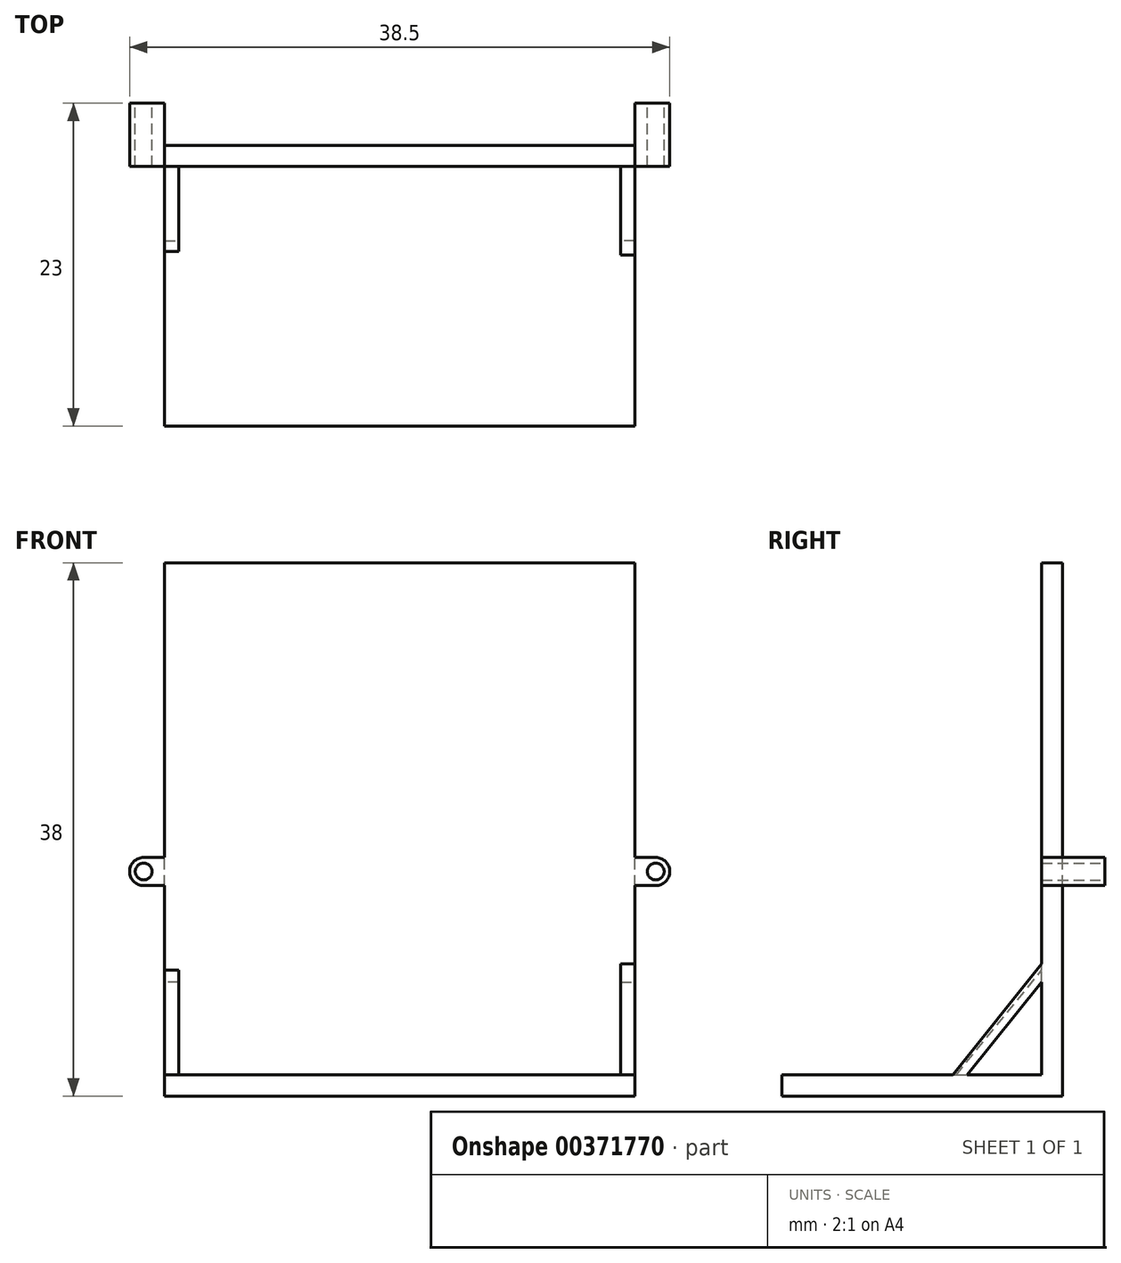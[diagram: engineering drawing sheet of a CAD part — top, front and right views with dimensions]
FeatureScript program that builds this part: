
annotation { "Feature Type Name" : "Feature", "Feature Type Description" : "" }
export const myFeature = defineFeature(function(context is Context, id is Id, definition is map)
    precondition{}
    {
        {
            var Q0;
            Q0=qCreatedBy(makeId("Front.planeOp"),FACE);
            var sketch = newSketch(context, id + "F0", { "sketchPlane" : qUnion([Q0])});
            skLineSegment(sketch, "E0.bottom", {"start": v(0, 0) * mm, "end": v(-33.5, 0) * mm});
            skLineSegment(sketch, "E0.top", {"start": v(0, 38) * mm, "end": v(-33.5, 38) * mm});
            skLineSegment(sketch, "E0.left", {"start": v(0, 0) * mm, "end": v(0, 38) * mm});
            skLineSegment(sketch, "E0.right", {"start": v(-33.5, 0) * mm, "end": v(-33.5, 38) * mm});
            skArc(sketch, "E1", {"start": v(-35, 17) * mm, "mid": v(-36, 16) * mm, "end": v(-35, 15) * mm});
            skLineSegment(sketch, "E2", {"start": v(-35, 17) * mm, "end": v(-33.5, 17) * mm});
            skLineSegment(sketch, "E3", {"start": v(-35, 15) * mm, "end": v(-33.5, 15) * mm});
            skLineSegment(sketch, "E4", {"start": v(-33.5, 15) * mm, "end": v(1.5, 15) * mm});
            skLineSegment(sketch, "E5", {"start": v(-33.5, 17) * mm, "end": v(1.5, 17) * mm});
            skArc(sketch, "E6", {"start": v(1.5, 15) * mm, "mid": v(2.5, 16) * mm, "end": v(1.5, 17) * mm});
            skCircle(sketch, "E7", {"center": v(1.5, 16) * mm, "radius": 0.6 * mm});
            skCircle(sketch, "E8", {"center": v(-35, 16) * mm, "radius": 0.6 * mm});
            skSolve(sketch);
        }
        {
            var Q0;
            Q0=qCreatedBy(makeId("Top.planeOp"),FACE);
            var sketch = newSketch(context, id + "F1", { "sketchPlane" : qUnion([Q0])});
            skLineSegment(sketch, "E9.bottom", {"start": v(-33.5, 0) * mm, "end": v(0, 0) * mm});
            skLineSegment(sketch, "E9.top", {"start": v(-33.5, -20) * mm, "end": v(0, -20) * mm});
            skLineSegment(sketch, "E9.left", {"start": v(-33.5, 0) * mm, "end": v(-33.5, -20) * mm});
            skLineSegment(sketch, "E9.right", {"start": v(0, 0) * mm, "end": v(0, -20) * mm});
            skSolve(sketch);
        }
        {
            var Q0;
            Q0=qCreatedBy(makeId("Right.planeOp"),FACE);
            var sketch = newSketch(context, id + "F2", { "sketchPlane" : qUnion([Q0])});
            skLineSegment(sketch, "E10", {"start": v(-8, 0) * mm, "end": v(0, 10) * mm});
            skLineSegment(sketch, "E11", {"start": v(0, 10) * mm, "end": v(0, 11.28) * mm});
            skLineSegment(sketch, "E12", {"start": v(0, 11.28) * mm, "end": v(-9.02, 0) * mm});
            skLineSegment(sketch, "E13", {"start": v(0, 11.28) * mm, "end": v(0, 10) * mm});
            skLineSegment(sketch, "E14", {"start": v(-8, 0) * mm, "end": v(-9.02, 0) * mm});
            skSolve(sketch);
        }
        {
            var Q0;
            {var subQ0=sQuery(id+"F0.wireOp",EDGE,"E0.top");Q0=makeQuery(id+"F0.imprint","IMPRINT",FACE,{"disambiguationData":[TD([[makeQuery(id+"F0.imprint","IMPRINT",EDGE,{"derivedFrom":subQ0}),1.0]])]});}
            var Q1;
            {var subQ0=sQuery(id+"F0.wireOp",EDGE,"E4");var subQ1=sQuery(id+"F0.wireOp",EDGE,"E0.left");var subQ2=makeQuery(id+"F0.imprint","INTERSECT",VERTEX,{"derivedFrom":[subQ1,subQ0]});Q1=makeQuery(id+"F0.imprint","IMPRINT",FACE,{"disambiguationData":[TD([[makeQuery(id+"F0.imprint","IMPRINT",EDGE,{"disambiguationData":[TD([[subQ2,-1.0]])],"derivedFrom":subQ1}),1.0]])]});}
            var Q2;
            {var subQ0=sQuery(id+"F0.wireOp",EDGE,"E0.bottom");Q2=makeQuery(id+"F0.imprint","IMPRINT",FACE,{"disambiguationData":[TD([[makeQuery(id+"F0.imprint","IMPRINT",EDGE,{"derivedFrom":subQ0}),-1.0]])]});}
            var Q3;
            Q3=makeQuery(id+"F0.imprint","IMPRINT",FACE,{"disambiguationData":[TD([[makeQuery(id+"F0.imprint","IMPRINT",EDGE,{"derivedFrom":sQuery(id+"F0.wireOp",EDGE,"E1")}),1.0]])]});
            var Q4;
            {var subQ0=sQuery(id+"F0.wireOp",EDGE,"E6");Q4=makeQuery(id+"F0.imprint","IMPRINT",FACE,{"disambiguationData":[TD([[makeQuery(id+"F0.imprint","IMPRINT",EDGE,{"derivedFrom":subQ0}),1.0]])]});}
            extrude(context, id + "F3", {"entities" : qUnion([Q0, Q1, Q2, Q3, Q4]), "depth" : 1.5 * mm});
        }
        {
            var Q0;
            Q0=makeQuery(id+"F1.imprint","IMPRINT",FACE,{"disambiguationData":[TD([[makeQuery(id+"F1.imprint","IMPRINT",EDGE,{"derivedFrom":sQuery(id+"F1.wireOp",EDGE,"E9.bottom")}),-1.0]])]});
            extrude(context, id + "F4", {"entities" : qUnion([Q0]), "operationType" : NewBodyOperationType.ADD, "depth" : 1.5 * mm});
        }
        {
            var Q0;
            Q0 = qSketchRegion(id + "F2", true);
            extrude(context, id + "F5", {"entities" : qUnion([Q0]), "operationType" : NewBodyOperationType.ADD, "oppositeDirection" : true, "depth" : 1 * mm});
        }
        {
            var Q0;
            Q0=qCreatedBy(makeId("Right.planeOp"),FACE);
            cPlane(context, id + "F6", {"entities" : qUnion([Q0]), "cplaneType" : CPlaneType.OFFSET, "offset" : 32.5 * mm, "oppositeDirection" : true, "width" : 150 * mm, "height" : 150 * mm});
        }
        {
            var Q0;
            Q0=qCreatedBy(id+"F6.planeOp",FACE);
            var sketch = newSketch(context, id + "F7", { "sketchPlane" : qUnion([Q0])});
            skLineSegment(sketch, "E15", {"start": v(-8, 0) * mm, "end": v(-8.8, 0) * mm});
            skLineSegment(sketch, "E16", {"start": v(-8.8, 0) * mm, "end": v(0, 10.8) * mm});
            skLineSegment(sketch, "E17", {"start": v(0, 10.8) * mm, "end": v(0, 10) * mm});
            skLineSegment(sketch, "E18", {"start": v(0, 10) * mm, "end": v(-8, 0) * mm});
            skSolve(sketch);
        }
        {
            var Q0;
            Q0=makeQuery(id+"F7.imprint","IMPRINT",FACE,{"disambiguationData":[TD([[makeQuery(id+"F7.imprint","IMPRINT",EDGE,{"derivedFrom":sQuery(id+"F7.wireOp",EDGE,"E15")}),-1.0]])]});
            extrude(context, id + "F8", {"entities" : qUnion([Q0]), "operationType" : NewBodyOperationType.ADD, "oppositeDirection" : true, "depth" : 1 * mm});
        }
        {
            var Q0;
            Q0=makeQuery(id+"F0.imprint","IMPRINT",FACE,{"disambiguationData":[TD([[makeQuery(id+"F0.imprint","IMPRINT",EDGE,{"derivedFrom":sQuery(id+"F0.wireOp",EDGE,"E1")}),1.0]])]});
            var Q1;
            {var subQ0=sQuery(id+"F0.wireOp",EDGE,"E6");Q1=makeQuery(id+"F0.imprint","IMPRINT",FACE,{"disambiguationData":[TD([[makeQuery(id+"F0.imprint","IMPRINT",EDGE,{"derivedFrom":subQ0}),1.0]])]});}
            extrude(context, id + "F9", {"entities" : qUnion([Q0, Q1]), "operationType" : NewBodyOperationType.ADD, "oppositeDirection" : true, "depth" : 3 * mm});
        }
    });
